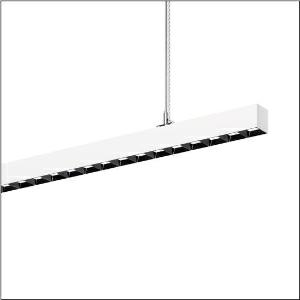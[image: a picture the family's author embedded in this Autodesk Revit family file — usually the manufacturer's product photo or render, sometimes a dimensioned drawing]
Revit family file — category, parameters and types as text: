
# Revit family: silica_r__21_51mx31dc3dwb_5f0e
name_source: partatom
category: Lighting Fixtures
units: mm (PartAtom-declared; Revit-internal decimal feet)

## family parameters
Cut with Voids When Loaded = No
Host = Face
Light Source = No
Part Type = Normal
Room Calculation Point = No
Round Connector Dimension = Use Diameter
Shared = No

## types (1)
- --- (1 x LED, 18230 lm, 113.3 W, 3000K)
    Apparent Load = 113 VA
    CIE Flux Codes = 87 99 100 59 100
    Color Rendering = 80
    Color Temperature = 3000K
    Default Elevation = 1800 mm
    Description = Silica® 21, office luminaire, primary light control with darklight reflector, of PMMA, black, CAT 2 (L<= 3000cd/m²), light emission: direct/indirect distribution, primary light characteristic: symmetric, installation type: suspended mounting, LED, rated luminous flux: 18.230lm, luminous efficacy: 161lm/W, light colour: 830, colour temperature: 3000K, with terminal, 3+2-pole, max. 2.5mm², mains connection: 220..240V, AC, 50/60Hz, rated input power: 113.3W, luminaire housing, of aluminium, traffic white (RAL 9016), length: 3.004mm, width: 53mm, height: 53mm, protection rating (complete): IP20, insulation class (complete): insulation class I (protective earthing), certification: CE, permissible operating ambient temperature: 0..+35°C, standard: EN 50419, packaging unit: 1 piece
    Height = 53 mm
    Lamp = 1 x LED
    Lamp Light Flux = 18230 lm
    Lamp Power = 113.3 W
    Lamp count = 1
    Length = 3004 mm
    Luminous efficacy = 161 lm/W
    Manufacturer = Siteco
    ModVariant = No
    Model = 51MX31DC3DWB
    Mounting Place = Ceiling
    Mounting Type = Pendant
    Number of Poles = 1
    OnlyDefault = Yes
    Power Factor = 1
    Product Name = Silica® 21
    Product group = office luminaire | ceiling pendant
    ProductGroupID = 902
    Protection Class = Protection class I
    Protection Degree = IP 20
    RLX_Detail_Level = 1
    RLX_Emergency_Light_Flux = 0 lm
    RLX_Emergency_Type = 0
    RLX_Emergency_Type_DB = No
    RlxData = <blob elided: 64109 chars, md5=34760a2e>
    Socket = socket
    Standby Power = 0 W
    System Light Flux = 18230 lm
    System Power = 113 W
    Type Comments = factory setting: luminous flux: 100 % | dim-lin: 254 | 392 mA
    Type Image = l_1313619.jpg
    URL = http://relux.com
    VarID = @adj_070039
    Voltage = 0 V
    Weight = 0.00 kg
    Width = 53 mm

## geometry (parser evidence)
native form markers: Blend x4, Sweep x12
no freeform markers — native parametric forms only
